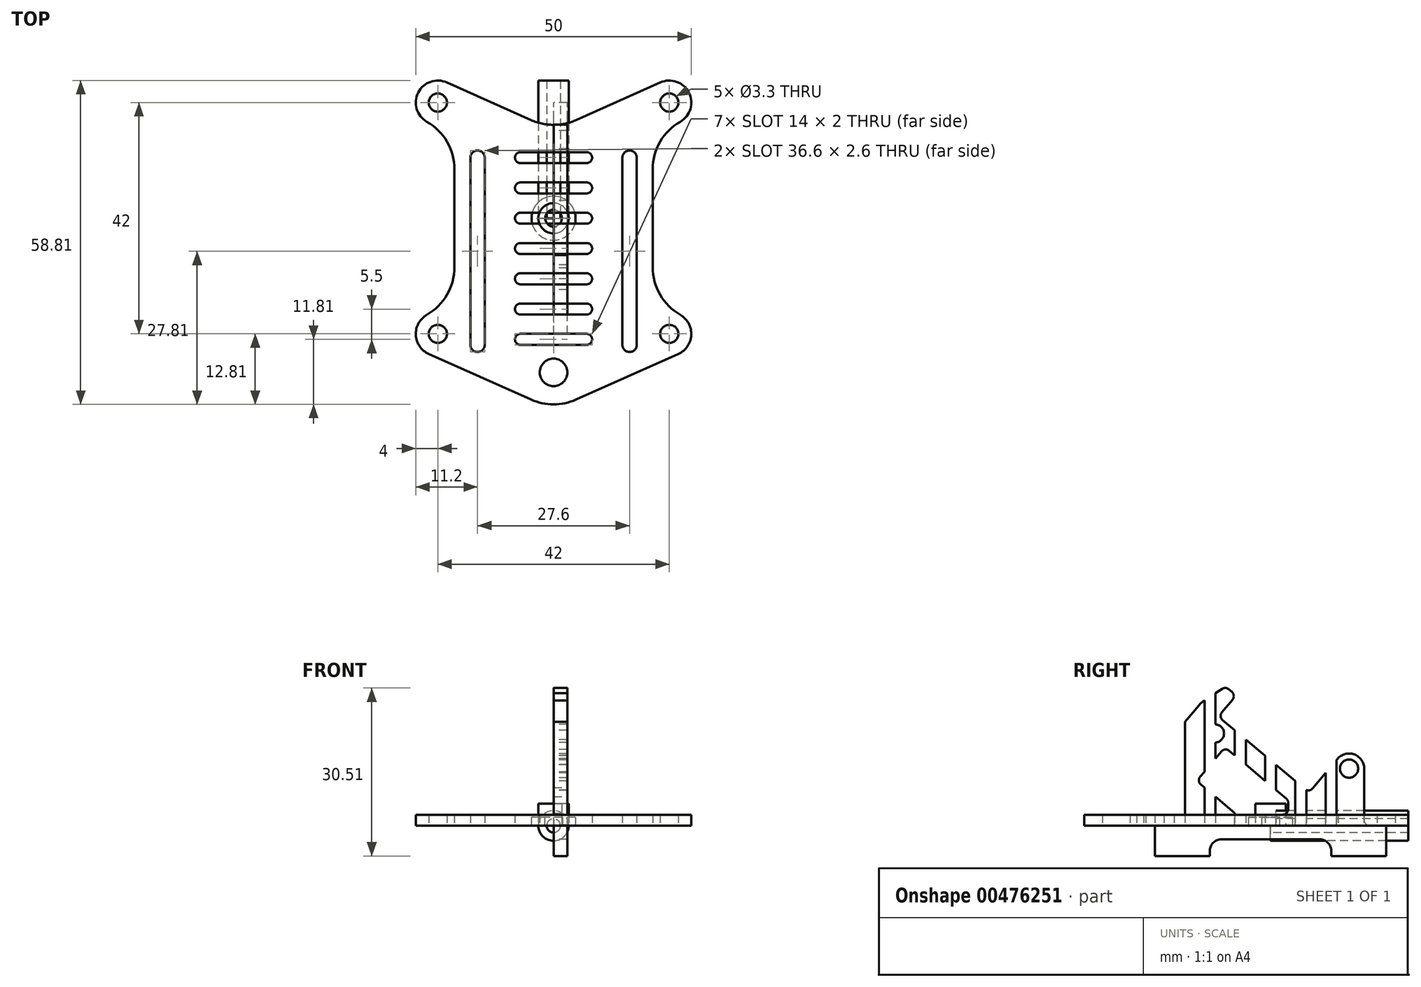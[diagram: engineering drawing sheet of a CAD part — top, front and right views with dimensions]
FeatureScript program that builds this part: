
annotation { "Feature Type Name" : "Feature", "Feature Type Description" : "" }
export const myFeature = defineFeature(function(context is Context, id is Id, definition is map)
    precondition{}
    {
        {
            var Q0;
            Q0=qCreatedBy(makeId("Right.planeOp"),FACE);
            var sketch = newSketch(context, id + "F0", { "sketchPlane" : qUnion([Q0])});
            skLineSegment(sketch, "E0.bottom", {"start": v(-21, 0) * mm, "end": v(-18, 0) * mm});
            skLineSegment(sketch, "E0.top", {"start": v(-21, -5.5) * mm, "end": v(-11, -5.5) * mm});
            skLineSegment(sketch, "E0.left", {"start": v(-21, 0) * mm, "end": v(-21, -5.5) * mm});
            skLineSegment(sketch, "E0.right", {"start": v(21, 0) * mm, "end": v(21, -5.5) * mm});
            skLineSegment(sketch, "E1.bottom", {"start": v(-8.7, 19.18) * mm, "end": v(6.24, 6.64) * mm});
            skLineSegment(sketch, "E1.left", {"start": v(-8.83, 20.59) * mm, "end": v(-6.9, 22.88) * mm});
            skPoint(sketch, "E1.middle", {"position": v(0.37, 14.83) * mm});
            skLineSegment(sketch, "E2", {"start": v(7.64, 6.77) * mm, "end": v(12.14, 12.13) * mm});
            skLineSegment(sketch, "E3", {"start": v(17, 10.36) * mm, "end": v(17, 1) * mm});
            skLineSegment(sketch, "E4", {"start": v(-7.02, 24.3) * mm, "end": v(-7.6, 24.78) * mm});
            skLineSegment(sketch, "E5", {"start": v(-8.8, 24.85) * mm, "end": v(-11.92, 22.8) * mm});
            skLineSegment(sketch, "E6", {"start": v(-13, 21.83) * mm, "end": v(-15.83, 18.46) * mm});
            skLineSegment(sketch, "E7", {"start": v(-17, 15.25) * mm, "end": v(-17, 1) * mm});
            skArc(sketch, "E8", {"start": v(17, 10.36) * mm, "mid": v(15.2, 12.94) * mm, "end": v(12.14, 12.13) * mm});
            skLineSegment(sketch, "E9", {"start": v(-7.5, 13.6) * mm, "end": v(2.86, 4.9) * mm});
            skLineSegment(sketch, "E10", {"start": v(-5.76, 2) * mm, "end": v(2.22, 2) * mm});
            skLineSegment(sketch, "E11", {"start": v(-6.4, 2.23) * mm, "end": v(-12.65, 7.48) * mm});
            skLineSegment(sketch, "E12", {"start": v(-12.77, 8.88) * mm, "end": v(-8.91, 13.48) * mm});
            skLineSegment(sketch, "E13", {"start": v(3.22, 4.14) * mm, "end": v(3.22, 3) * mm});
            skLineSegment(sketch, "E14.trimOffspring", {"start": v(18, 0) * mm, "end": v(21, 0) * mm});
            skCircle(sketch, "E15", {"center": v(-10.09, 16.75) * mm, "radius": 1.65 * mm});
            skCircle(sketch, "E16", {"center": v(-10.09, 16.75) * mm, "radius": 2.75 * mm, "construction": true});
            skPoint(sketch, "E17.visualSharp", {"position": v(-8.27, 14.25) * mm});
            skArc(sketch, "E17.filletArc", {"start": v(-7.5, 13.6) * mm, "mid": v(-8.24, 13.83) * mm, "end": v(-8.91, 13.48) * mm});
            skPoint(sketch, "E18.visualSharp", {"position": v(3.22, 4.6) * mm});
            skArc(sketch, "E18.filletArc", {"start": v(3.22, 4.14) * mm, "mid": v(3.13, 4.56) * mm, "end": v(2.86, 4.9) * mm});
            skPoint(sketch, "E19.visualSharp", {"position": v(3.22, 2) * mm});
            skArc(sketch, "E19.filletArc", {"start": v(2.22, 2) * mm, "mid": v(2.93, 2.3) * mm, "end": v(3.22, 3) * mm});
            skPoint(sketch, "E20.visualSharp", {"position": v(-6.12, 2) * mm});
            skArc(sketch, "E20.filletArc", {"start": v(-6.4, 2.23) * mm, "mid": v(-6.1, 2.06) * mm, "end": v(-5.76, 2) * mm});
            skPoint(sketch, "E21.visualSharp", {"position": v(-13.41, 8.12) * mm});
            skArc(sketch, "E21.filletArc", {"start": v(-12.77, 8.88) * mm, "mid": v(-13, 8.15) * mm, "end": v(-12.65, 7.48) * mm});
            skPoint(sketch, "E22.visualSharp", {"position": v(17, 0) * mm});
            skArc(sketch, "E22.filletArc", {"start": v(17, 1) * mm, "mid": v(17.3, 0.3) * mm, "end": v(18, 0) * mm});
            skPoint(sketch, "E23.visualSharp", {"position": v(-17, 0) * mm});
            skArc(sketch, "E23.filletArc", {"start": v(-18, 0) * mm, "mid": v(-17.3, 0.3) * mm, "end": v(-17, 1) * mm});
            skPoint(sketch, "E24.visualSharp", {"position": v(-17, 17.07) * mm});
            skArc(sketch, "E24.filletArc", {"start": v(-15.83, 18.46) * mm, "mid": v(-16.7, 16.96) * mm, "end": v(-17, 15.25) * mm});
            skPoint(sketch, "E25.visualSharp", {"position": v(-12.53, 22.4) * mm});
            skArc(sketch, "E25.filletArc", {"start": v(-11.92, 22.8) * mm, "mid": v(-12.5, 22.35) * mm, "end": v(-13, 21.83) * mm});
            skPoint(sketch, "E26.visualSharp", {"position": v(-8.17, 25.26) * mm});
            skArc(sketch, "E26.filletArc", {"start": v(-7.6, 24.78) * mm, "mid": v(-8.18, 25.01) * mm, "end": v(-8.8, 24.85) * mm});
            skPoint(sketch, "E27.visualSharp", {"position": v(-6.25, 23.65) * mm});
            skArc(sketch, "E27.filletArc", {"start": v(-6.9, 22.88) * mm, "mid": v(-6.67, 23.61) * mm, "end": v(-7.02, 24.3) * mm});
            skPoint(sketch, "E28.visualSharp", {"position": v(-9.47, 19.82) * mm});
            skArc(sketch, "E28.filletArc", {"start": v(-8.83, 20.59) * mm, "mid": v(-9.06, 19.86) * mm, "end": v(-8.7, 19.18) * mm});
            skPoint(sketch, "E29.visualSharp", {"position": v(7, 6) * mm});
            skArc(sketch, "E29.filletArc", {"start": v(6.24, 6.64) * mm, "mid": v(6.96, 6.41) * mm, "end": v(7.64, 6.77) * mm});
            skCircle(sketch, "E30", {"center": v(14.25, 10.36) * mm, "radius": 1.65 * mm});
            skLineSegment(sketch, "E31", {"start": v(-11, -5.5) * mm, "end": v(-11, -4.5) * mm});
            skLineSegment(sketch, "E32", {"start": v(-9, -2.5) * mm, "end": v(9, -2.5) * mm});
            skLineSegment(sketch, "E33", {"start": v(11, -4.5) * mm, "end": v(11, -5.5) * mm});
            skLineSegment(sketch, "E34.trimOffspring", {"start": v(11, -5.5) * mm, "end": v(21, -5.5) * mm});
            skPoint(sketch, "E35.visualSharp", {"position": v(-11, -2.5) * mm});
            skArc(sketch, "E35.filletArc", {"start": v(-9, -2.5) * mm, "mid": v(-10.41, -3.09) * mm, "end": v(-11, -4.5) * mm});
            skPoint(sketch, "E36.visualSharp", {"position": v(11, -2.5) * mm});
            skArc(sketch, "E36.filletArc", {"start": v(11, -4.5) * mm, "mid": v(10.41, -3.09) * mm, "end": v(9, -2.5) * mm});
            skSolve(sketch);
        }
        {
            var Q0;
            Q0=makeQuery(id+"F0.imprint","IMPRINT",FACE,{"disambiguationData":[TD([[makeQuery(id+"F0.imprint","IMPRINT",EDGE,{"derivedFrom":sQuery(id+"F0.wireOp",EDGE,"E0.bottom")}),-1.0]])]});
            extrude(context, id + "F1", {"entities" : qUnion([Q0]), "depth" : 2.5 * mm, "offsetDistance" : 25 * mm});
        }
        {
            var Q0;
            Q0=qCreatedBy(makeId("Top.planeOp"),FACE);
            var sketch = newSketch(context, id + "F2", { "sketchPlane" : qUnion([Q0])});
            skCircle(sketch, "E37", {"center": v(-21, 21) * mm, "radius": 1.65 * mm});
            skCircle(sketch, "E38.MirrorC", {"center": v(21, 21) * mm, "radius": 1.65 * mm});
            skCircle(sketch, "E39.MirrorC", {"center": v(-21, -21) * mm, "radius": 1.65 * mm});
            skCircle(sketch, "E40.MirrorC", {"center": v(21, -21) * mm, "radius": 1.65 * mm});
            skArc(sketch, "E41", {"start": v(-19.37, 24.65) * mm, "mid": v(-24.56, 22.82) * mm, "end": v(-23, 17.54) * mm});
            skArc(sketch, "E42", {"start": v(-23, -17.54) * mm, "mid": v(-25, -21.2) * mm, "end": v(-22.63, -24.65) * mm});
            skArc(sketch, "E43", {"start": v(23, 17.54) * mm, "mid": v(24.56, 22.82) * mm, "end": v(19.37, 24.65) * mm});
            skArc(sketch, "E44", {"start": v(22.63, -24.65) * mm, "mid": v(25, -21.2) * mm, "end": v(23, -17.54) * mm});
            skLineSegment(sketch, "E45", {"start": v(-18, 8.88) * mm, "end": v(-18, -8.88) * mm});
            skLineSegment(sketch, "E46", {"start": v(18, 8.88) * mm, "end": v(18, -8.88) * mm});
            skArc(sketch, "E47", {"start": v(-18, 8.88) * mm, "mid": v(-19.34, 13.88) * mm, "end": v(-23, 17.54) * mm});
            skArc(sketch, "E48", {"start": v(-23, -17.54) * mm, "mid": v(-19.34, -13.88) * mm, "end": v(-18, -8.88) * mm});
            skArc(sketch, "E49", {"start": v(18, -8.88) * mm, "mid": v(19.34, -13.88) * mm, "end": v(23, -17.54) * mm});
            skArc(sketch, "E50", {"start": v(23, 17.54) * mm, "mid": v(19.34, 13.88) * mm, "end": v(18, 8.88) * mm});
            skLineSegment(sketch, "E51", {"start": v(-13.8, 11) * mm, "end": v(-13.8, -23) * mm, "construction": true});
            skArc(sketch, "E52.0.startCap", {"start": v(-15.1, 11) * mm, "mid": v(-13.8, 12.3) * mm, "end": v(-12.5, 11) * mm});
            skArc(sketch, "E52.0.endCap", {"start": v(-12.5, -23) * mm, "mid": v(-13.8, -24.3) * mm, "end": v(-15.1, -23) * mm});
            skLineSegment(sketch, "E52.0.left", {"start": v(-12.5, 11) * mm, "end": v(-12.5, -23) * mm});
            skLineSegment(sketch, "E52.0.right", {"start": v(-15.1, 11) * mm, "end": v(-15.1, -23) * mm});
            skArc(sketch, "E53.MirrorCS", {"start": v(15.1, 11) * mm, "mid": v(13.8, 12.3) * mm, "end": v(12.5, 11) * mm});
            skLineSegment(sketch, "E54.MirrorCS", {"start": v(15.1, 11) * mm, "end": v(15.1, -23) * mm});
            skArc(sketch, "E55.MirrorCS", {"start": v(12.5, -23) * mm, "mid": v(13.8, -24.3) * mm, "end": v(15.1, -23) * mm});
            skLineSegment(sketch, "E56.MirrorCS", {"start": v(13.8, 11) * mm, "end": v(13.8, -23) * mm, "construction": true});
            skLineSegment(sketch, "E57.MirrorCS", {"start": v(12.5, 11) * mm, "end": v(12.5, -23) * mm});
            skLineSegment(sketch, "E58", {"start": v(-19.37, 24.65) * mm, "end": v(-4.08, 17.82) * mm});
            skLineSegment(sketch, "E59", {"start": v(4.08, 17.82) * mm, "end": v(19.37, 24.65) * mm});
            skPoint(sketch, "E60.visualSharp", {"position": v(0, 16) * mm});
            skArc(sketch, "E60.filletArc", {"start": v(-4.08, 17.82) * mm, "mid": v(0, 16.95) * mm, "end": v(4.08, 17.82) * mm});
            skLineSegment(sketch, "E61", {"start": v(-22.63, -24.65) * mm, "end": v(-4.08, -32.94) * mm});
            skLineSegment(sketch, "E62", {"start": v(4.08, -32.94) * mm, "end": v(22.63, -24.65) * mm});
            skPoint(sketch, "E63.visualSharp", {"position": v(0, -34.76) * mm});
            skArc(sketch, "E63.filletArc", {"start": v(-4.08, -32.94) * mm, "mid": v(0, -33.8) * mm, "end": v(4.08, -32.94) * mm});
            skSolve(sketch);
        }
        {
            var Q0;
            Q0=makeQuery(id+"F2.imprint","IMPRINT",FACE,{"disambiguationData":[TD([[makeQuery(id+"F2.imprint","IMPRINT",EDGE,{"derivedFrom":sQuery(id+"F2.wireOp",EDGE,"E37")}),-1.0]])]});
            extrude(context, id + "F3", {"entities" : qUnion([Q0]), "depth" : 2 * mm, "offsetDistance" : 25 * mm});
        }
        {
            var Q0;
            Q0=qCreatedBy(makeId("Top.planeOp"),FACE);
            var sketch = newSketch(context, id + "F4", { "sketchPlane" : qUnion([Q0])});
            skLineSegment(sketch, "E64", {"start": v(0, 0) * mm, "end": v(0, 25) * mm, "construction": true});
            skLineSegment(sketch, "E65", {"start": v(1.25, 25) * mm, "end": v(2.75, 25) * mm});
            skLineSegment(sketch, "E66", {"start": v(2.75, 25) * mm, "end": v(2.75, 0) * mm});
            skLineSegment(sketch, "E67", {"start": v(2.75, 0) * mm, "end": v(1.25, 0) * mm});
            skLineSegment(sketch, "E68", {"start": v(1.25, 25) * mm, "end": v(1.25, 0) * mm});
            skSolve(sketch);
        }
        {
            var Q0;
            Q0=makeQuery(id+"F4.imprint","IMPRINT",FACE,{"disambiguationData":[TD([[makeQuery(id+"F4.imprint","IMPRINT",EDGE,{"derivedFrom":sQuery(id+"F4.wireOp",EDGE,"E65")}),-1.0]])]});
            var Q1;
            Q1=sQuery(id+"F4.wireOp",EDGE,"E64");
            revolve(context, id + "F5", {"entities" : qUnion([Q0]), "axis" : qUnion([Q1]), "revolveType" : RevolveType.FULL});
        }
        {
            var Q0;
            Q0=makeQuery(id+"F3.opExtrude","CAP_FACE",FACE,{"disambiguationData":[OSD([sQuery(id+"F2.wireOp",EDGE,"E37"),sQuery(id+"F2.wireOp",EDGE,"E38.MirrorC"),sQuery(id+"F2.wireOp",EDGE,"E39.MirrorC"),sQuery(id+"F2.wireOp",EDGE,"E40.MirrorC"),sQuery(id+"F2.wireOp",EDGE,"E41"),sQuery(id+"F2.wireOp",EDGE,"E42"),sQuery(id+"F2.wireOp",EDGE,"E43"),sQuery(id+"F2.wireOp",EDGE,"E44"),sQuery(id+"F2.wireOp",EDGE,"HbRvRGti-VTHd-3TSI-MkX5-C2cFPtapRuhi"),sQuery(id+"F2.wireOp",EDGE,"Mz0DYlBK-cip7-vn1s-uTGy-A6edBpfErfw1"),sQuery(id+"F2.wireOp",EDGE,"E45"),sQuery(id+"F2.wireOp",EDGE,"E46"),sQuery(id+"F2.wireOp",EDGE,"E47"),sQuery(id+"F2.wireOp",EDGE,"E48"),sQuery(id+"F2.wireOp",EDGE,"E49"),sQuery(id+"F2.wireOp",EDGE,"E50"),sQuery(id+"F2.wireOp",EDGE,"E52.0.startCap"),sQuery(id+"F2.wireOp",EDGE,"E52.0.endCap"),sQuery(id+"F2.wireOp",EDGE,"E52.0.left"),sQuery(id+"F2.wireOp",EDGE,"E52.0.right"),sQuery(id+"F2.wireOp",EDGE,"E53.MirrorCS"),sQuery(id+"F2.wireOp",EDGE,"E54.MirrorCS"),sQuery(id+"F2.wireOp",EDGE,"E55.MirrorCS"),sQuery(id+"F2.wireOp",EDGE,"E57.MirrorCS")])],"isStart":true});
            var sketch = newSketch(context, id + "F6", { "sketchPlane" : qUnion([Q0])});
            skLineSegment(sketch, "E69", {"start": v(-6, 22) * mm, "end": v(6, 22) * mm, "construction": true});
            skArc(sketch, "E70.0.startCap", {"start": v(-6, 21) * mm, "mid": v(-7, 22) * mm, "end": v(-6, 23) * mm});
            skArc(sketch, "E70.0.endCap", {"start": v(6, 23) * mm, "mid": v(7, 22) * mm, "end": v(6, 21) * mm});
            skLineSegment(sketch, "E70.0.left", {"start": v(-6, 23) * mm, "end": v(6, 23) * mm});
            skLineSegment(sketch, "E70.0.right", {"start": v(-6, 21) * mm, "end": v(6, 21) * mm});
            skArc(sketch, "E71.0.1.0", {"start": v(-6, 15.5) * mm, "mid": v(-7, 16.5) * mm, "end": v(-6, 17.5) * mm});
            skArc(sketch, "E71.0.1.1", {"start": v(6, 17.5) * mm, "mid": v(7, 16.5) * mm, "end": v(6, 15.5) * mm});
            skLineSegment(sketch, "E71.0.1.2", {"start": v(-6, 15.5) * mm, "end": v(6, 15.5) * mm});
            skLineSegment(sketch, "E71.0.1.3", {"start": v(-6, 17.5) * mm, "end": v(6, 17.5) * mm});
            skLineSegment(sketch, "E71.0.1.4", {"start": v(-6, 16.5) * mm, "end": v(6, 16.5) * mm, "construction": true});
            skArc(sketch, "E71.0.2.0", {"start": v(-6, 10) * mm, "mid": v(-7, 11) * mm, "end": v(-6, 12) * mm});
            skArc(sketch, "E71.0.2.1", {"start": v(6, 12) * mm, "mid": v(7, 11) * mm, "end": v(6, 10) * mm});
            skLineSegment(sketch, "E71.0.2.2", {"start": v(-6, 10) * mm, "end": v(6, 10) * mm});
            skLineSegment(sketch, "E71.0.2.3", {"start": v(-6, 12) * mm, "end": v(6, 12) * mm});
            skLineSegment(sketch, "E71.0.2.4", {"start": v(-6, 11) * mm, "end": v(6, 11) * mm, "construction": true});
            skArc(sketch, "E71.0.3.0", {"start": v(-6, 4.5) * mm, "mid": v(-7, 5.5) * mm, "end": v(-6, 6.5) * mm});
            skArc(sketch, "E71.0.3.1", {"start": v(6, 6.5) * mm, "mid": v(7, 5.5) * mm, "end": v(6, 4.5) * mm});
            skLineSegment(sketch, "E71.0.3.2", {"start": v(-6, 4.5) * mm, "end": v(6, 4.5) * mm});
            skLineSegment(sketch, "E71.0.3.3", {"start": v(-6, 6.5) * mm, "end": v(6, 6.5) * mm});
            skLineSegment(sketch, "E71.0.3.4", {"start": v(-6, 5.5) * mm, "end": v(6, 5.5) * mm, "construction": true});
            skArc(sketch, "E71.0.4.0", {"start": v(-6, -1) * mm, "mid": v(-7, 0) * mm, "end": v(-6, 1) * mm});
            skArc(sketch, "E71.0.4.1", {"start": v(6, 1) * mm, "mid": v(7, 0) * mm, "end": v(6, -1) * mm});
            skLineSegment(sketch, "E71.0.4.2", {"start": v(-6, -1) * mm, "end": v(6, -1) * mm});
            skLineSegment(sketch, "E71.0.4.3", {"start": v(-6, 1) * mm, "end": v(6, 1) * mm});
            skLineSegment(sketch, "E71.0.4.4", {"start": v(-6, 0) * mm, "end": v(6, 0) * mm, "construction": true});
            skArc(sketch, "E71.0.5.0", {"start": v(-6, -6.5) * mm, "mid": v(-7, -5.5) * mm, "end": v(-6, -4.5) * mm});
            skArc(sketch, "E71.0.5.1", {"start": v(6, -4.5) * mm, "mid": v(7, -5.5) * mm, "end": v(6, -6.5) * mm});
            skLineSegment(sketch, "E71.0.5.2", {"start": v(-6, -6.5) * mm, "end": v(6, -6.5) * mm});
            skLineSegment(sketch, "E71.0.5.3", {"start": v(-6, -4.5) * mm, "end": v(6, -4.5) * mm});
            skLineSegment(sketch, "E71.0.5.4", {"start": v(-6, -5.5) * mm, "end": v(6, -5.5) * mm, "construction": true});
            skArc(sketch, "E71.0.6.0", {"start": v(-6, -12) * mm, "mid": v(-7, -11) * mm, "end": v(-6, -10) * mm});
            skArc(sketch, "E71.0.6.1", {"start": v(6, -10) * mm, "mid": v(7, -11) * mm, "end": v(6, -12) * mm});
            skLineSegment(sketch, "E71.0.6.2", {"start": v(-6, -12) * mm, "end": v(6, -12) * mm});
            skLineSegment(sketch, "E71.0.6.3", {"start": v(-6, -10) * mm, "end": v(6, -10) * mm});
            skLineSegment(sketch, "E71.0.6.4", {"start": v(-6, -11) * mm, "end": v(6, -11) * mm, "construction": true});
            skLineSegment(sketch, "E71.direction1", {"start": v(-6, 21) * mm, "end": v(19, 21) * mm, "construction": true});
            skLineSegment(sketch, "E71.direction2", {"start": v(-6, 21) * mm, "end": v(-6, 15.5) * mm, "construction": true});
            skCircle(sketch, "E72", {"center": v(0, 28) * mm, "radius": 2.5 * mm});
            skSolve(sketch);
        }
        {
            var Q0;
            Q0=qSketchRegion(id+"F6",true);
            extrude(context, id + "F7", {"entities" : qUnion([Q0]), "operationType" : NewBodyOperationType.REMOVE, "oppositeDirection" : true, "depth" : 25 * mm, "offsetDistance" : 25 * mm});
        }
        {
            var Q0;
            Q0=qCreatedBy(makeId("Top.planeOp"),FACE);
            var sketch = newSketch(context, id + "F8", { "sketchPlane" : qUnion([Q0])});
            skCircle(sketch, "E73", {"center": v(0, 0) * mm, "radius": 2.75 * mm});
            skCircle(sketch, "E74", {"center": v(0, 0) * mm, "radius": 1.5 * mm});
            skSolve(sketch);
        }
        {
            var Q0;
            Q0=makeQuery(id+"F8.imprint","IMPRINT",FACE,{"disambiguationData":[TD([[makeQuery(id+"F8.imprint","IMPRINT",EDGE,{"derivedFrom":sQuery(id+"F8.wireOp",EDGE,"E73")}),1.0]])]});
            extrude(context, id + "F9", {"entities" : qUnion([Q0]), "depth" : 4 * mm, "offsetDistance" : 25 * mm});
        }
        {
            var Q0;
            Q0=qCreatedBy(makeId("Top.planeOp"),FACE);
            var sketch = newSketch(context, id + "F10", { "sketchPlane" : qUnion([Q0])});
            skCircle(sketch, "E75", {"center": v(0, 0) * mm, "radius": 4 * mm});
            skCircle(sketch, "E76", {"center": v(0, 0) * mm, "radius": 1.65 * mm});
            skSolve(sketch);
        }
        {
            var Q0;
            Q0=makeQuery(id+"F10.imprint","IMPRINT",FACE,{"disambiguationData":[TD([[makeQuery(id+"F10.imprint","IMPRINT",EDGE,{"derivedFrom":sQuery(id+"F10.wireOp",EDGE,"E75")}),1.0]])]});
            extrude(context, id + "F11", {"entities" : qUnion([Q0]), "depth" : 1.5 * mm, "offsetDistance" : 25 * mm});
        }
    });
